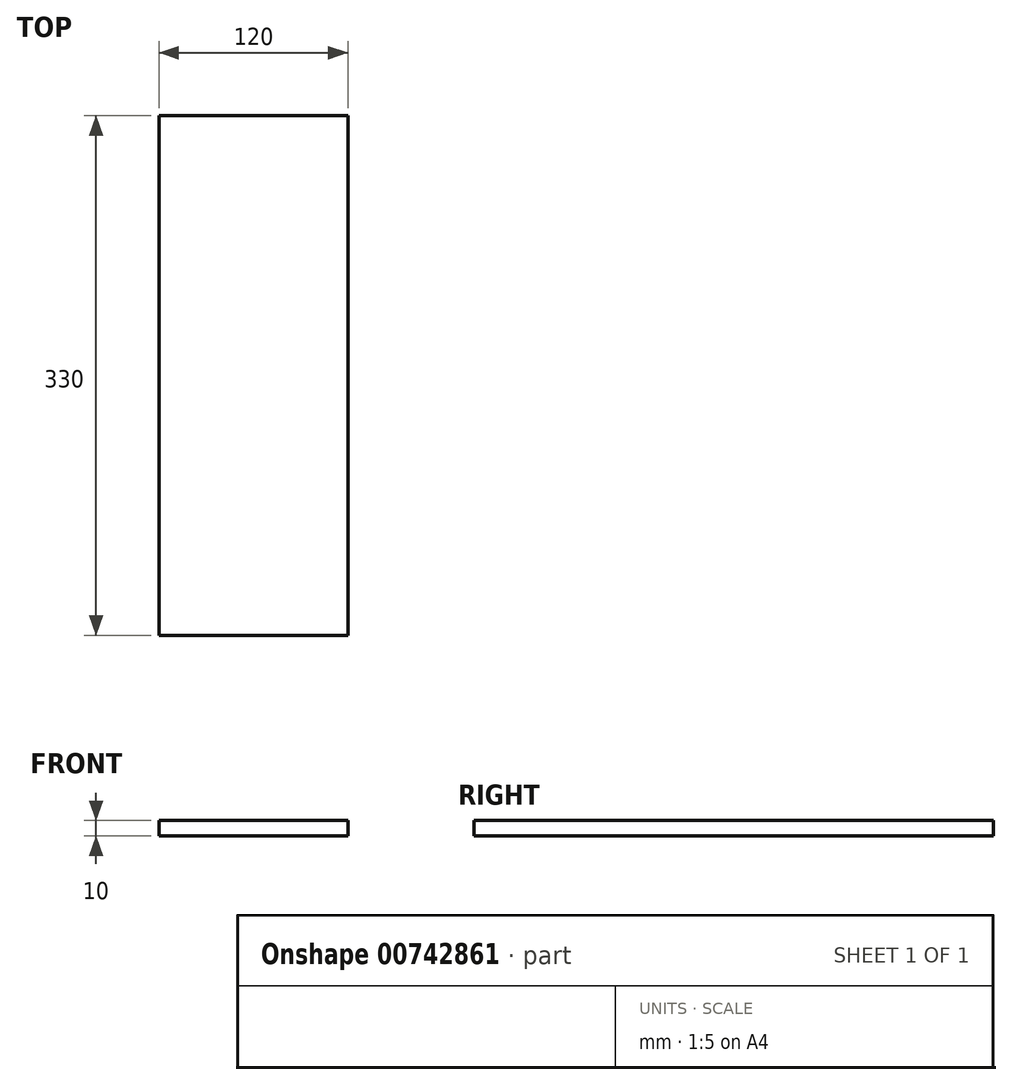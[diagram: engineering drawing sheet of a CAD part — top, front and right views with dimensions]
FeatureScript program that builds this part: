
annotation { "Feature Type Name" : "Feature", "Feature Type Description" : "" }
export const myFeature = defineFeature(function(context is Context, id is Id, definition is map)
    precondition{}
    {
        {
            var Q0;
            Q0=qCreatedBy(makeId("Top.planeOp"),FACE);
            var sketch = newSketch(context, id + "F0", { "sketchPlane" : qUnion([Q0])});
            skLineSegment(sketch, "E0.bottom", {"start": v(60, 165) * mm, "end": v(-60, 165) * mm});
            skLineSegment(sketch, "E0.top", {"start": v(60, -165) * mm, "end": v(-60, -165) * mm});
            skLineSegment(sketch, "E0.left", {"start": v(60, 165) * mm, "end": v(60, -165) * mm});
            skLineSegment(sketch, "E0.right", {"start": v(-60, 165) * mm, "end": v(-60, -165) * mm});
            skPoint(sketch, "E0.middle", {"position": v(0, 0) * mm});
            skSolve(sketch);
        }
        {
            var Q0;
            Q0=makeQuery(id+"F0.imprint","IMPRINT",FACE,{"disambiguationData":[TD([[makeQuery(id+"F0.imprint","IMPRINT",EDGE,{"derivedFrom":sQuery(id+"F0.wireOp",EDGE,"E0.bottom")}),1.0]])]});
            extrude(context, id + "F1", {"entities" : qUnion([Q0]), "endBound" : BoundingType.SYMMETRIC, "depth" : 10 * mm, "offsetDistance" : 25.4 * mm});
        }
    });
